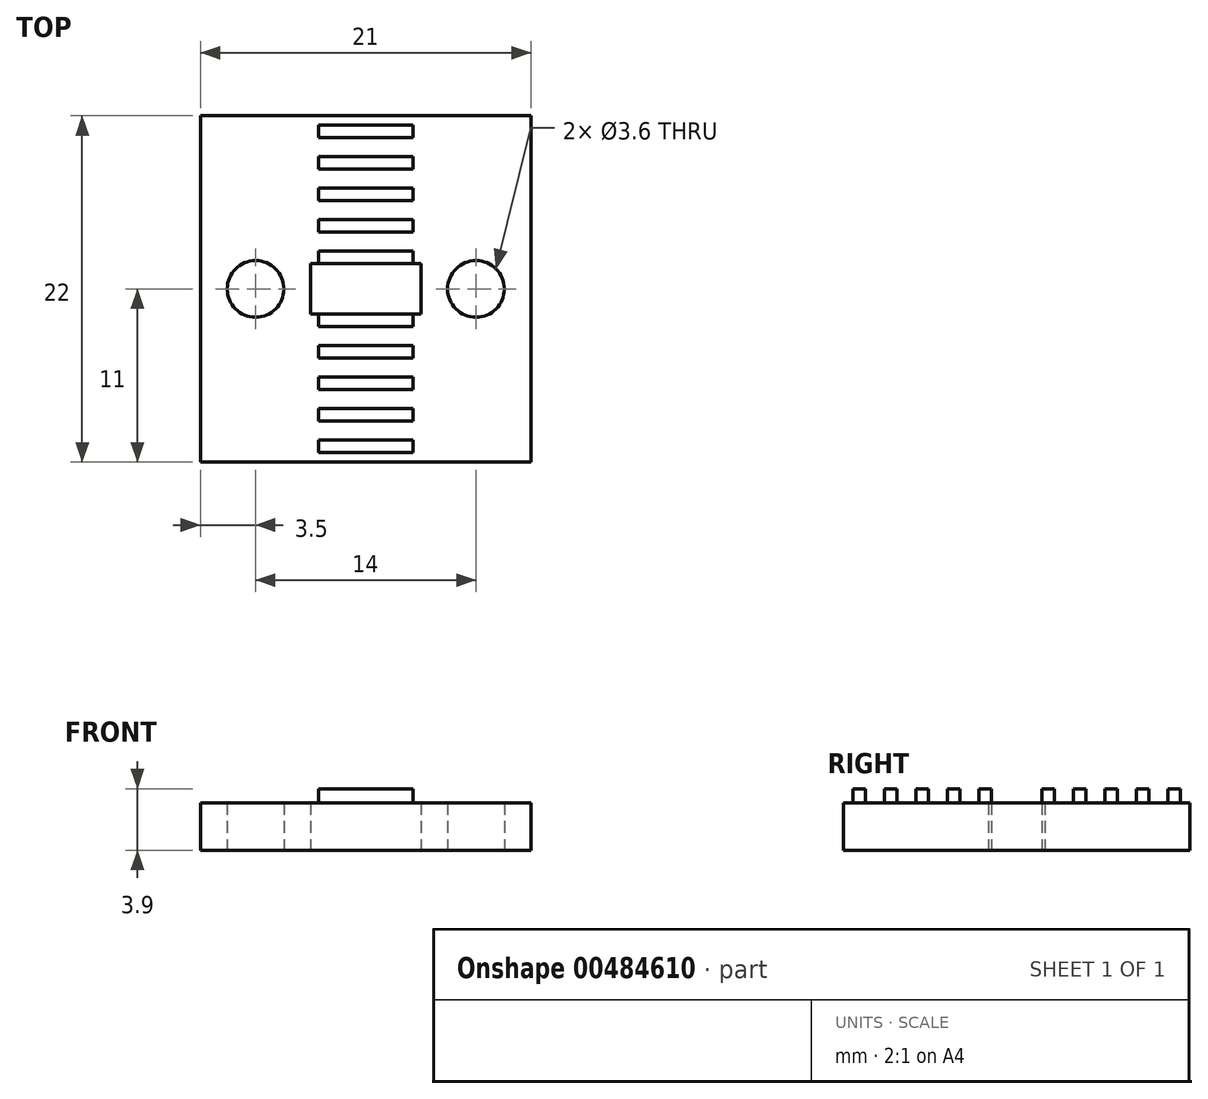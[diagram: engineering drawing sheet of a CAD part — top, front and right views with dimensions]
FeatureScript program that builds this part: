
annotation { "Feature Type Name" : "Feature", "Feature Type Description" : "" }
export const myFeature = defineFeature(function(context is Context, id is Id, definition is map)
    precondition{}
    {
        {
            var Q0;
            Q0=qCreatedBy(makeId("Top.planeOp"),FACE);
            var sketch = newSketch(context, id + "F0", { "sketchPlane" : qUnion([Q0])});
            skLineSegment(sketch, "E0", {"start": v(-20.99, 0) * mm, "end": v(23.9, 0) * mm, "construction": true});
            skCircle(sketch, "E1", {"center": v(-7, 0) * mm, "radius": 1.8 * mm});
            skCircle(sketch, "E2", {"center": v(7, 0) * mm, "radius": 1.8 * mm});
            skLineSegment(sketch, "E3", {"start": v(0, 19.46) * mm, "end": v(0, -20.23) * mm, "construction": true});
            skLineSegment(sketch, "E4.bottom", {"start": v(-3, 0.4) * mm, "end": v(3, 0.4) * mm});
            skLineSegment(sketch, "E4.top", {"start": v(-3, -0.4) * mm, "end": v(3, -0.4) * mm});
            skLineSegment(sketch, "E4.left", {"start": v(-3, 0.4) * mm, "end": v(-3, -0.4) * mm});
            skLineSegment(sketch, "E4.right", {"start": v(3, 0.4) * mm, "end": v(3, -0.4) * mm});
            skLineSegment(sketch, "E5.1.0.0", {"start": v(-3, -2.4) * mm, "end": v(3, -2.4) * mm});
            skLineSegment(sketch, "E5.1.0.1", {"start": v(-3, -1.6) * mm, "end": v(3, -1.6) * mm});
            skLineSegment(sketch, "E5.1.0.2", {"start": v(-3, -1.6) * mm, "end": v(-3, -2.4) * mm});
            skLineSegment(sketch, "E5.1.0.3", {"start": v(3, -1.6) * mm, "end": v(3, -2.4) * mm});
            skLineSegment(sketch, "E5.2.0.0", {"start": v(-3, -4.4) * mm, "end": v(3, -4.4) * mm});
            skLineSegment(sketch, "E5.2.0.1", {"start": v(-3, -3.6) * mm, "end": v(3, -3.6) * mm});
            skLineSegment(sketch, "E5.2.0.2", {"start": v(-3, -3.6) * mm, "end": v(-3, -4.4) * mm});
            skLineSegment(sketch, "E5.2.0.3", {"start": v(3, -3.6) * mm, "end": v(3, -4.4) * mm});
            skLineSegment(sketch, "E5.3.0.0", {"start": v(-3, -6.4) * mm, "end": v(3, -6.4) * mm});
            skLineSegment(sketch, "E5.3.0.1", {"start": v(-3, -5.6) * mm, "end": v(3, -5.6) * mm});
            skLineSegment(sketch, "E5.3.0.2", {"start": v(-3, -5.6) * mm, "end": v(-3, -6.4) * mm});
            skLineSegment(sketch, "E5.3.0.3", {"start": v(3, -5.6) * mm, "end": v(3, -6.4) * mm});
            skLineSegment(sketch, "E5.4.0.0", {"start": v(-3, -8.4) * mm, "end": v(3, -8.4) * mm});
            skLineSegment(sketch, "E5.4.0.1", {"start": v(-3, -7.6) * mm, "end": v(3, -7.6) * mm});
            skLineSegment(sketch, "E5.4.0.2", {"start": v(-3, -7.6) * mm, "end": v(-3, -8.4) * mm});
            skLineSegment(sketch, "E5.4.0.3", {"start": v(3, -7.6) * mm, "end": v(3, -8.4) * mm});
            skLineSegment(sketch, "E5.direction1", {"start": v(-3, -0.4) * mm, "end": v(-3, -2.4) * mm, "construction": true});
            skLineSegment(sketch, "E6.1.0.0", {"start": v(-3, 1.6) * mm, "end": v(3, 1.6) * mm});
            skLineSegment(sketch, "E6.1.0.1", {"start": v(-3, 2.4) * mm, "end": v(3, 2.4) * mm});
            skLineSegment(sketch, "E6.1.0.2", {"start": v(-3, 2.4) * mm, "end": v(-3, 1.6) * mm});
            skLineSegment(sketch, "E6.1.0.3", {"start": v(3, 2.4) * mm, "end": v(3, 1.6) * mm});
            skLineSegment(sketch, "E6.2.0.0", {"start": v(-3, 3.6) * mm, "end": v(3, 3.6) * mm});
            skLineSegment(sketch, "E6.2.0.1", {"start": v(-3, 4.4) * mm, "end": v(3, 4.4) * mm});
            skLineSegment(sketch, "E6.2.0.2", {"start": v(-3, 4.4) * mm, "end": v(-3, 3.6) * mm});
            skLineSegment(sketch, "E6.2.0.3", {"start": v(3, 4.4) * mm, "end": v(3, 3.6) * mm});
            skLineSegment(sketch, "E6.3.0.0", {"start": v(-3, 5.6) * mm, "end": v(3, 5.6) * mm});
            skLineSegment(sketch, "E6.3.0.1", {"start": v(-3, 6.4) * mm, "end": v(3, 6.4) * mm});
            skLineSegment(sketch, "E6.3.0.2", {"start": v(-3, 6.4) * mm, "end": v(-3, 5.6) * mm});
            skLineSegment(sketch, "E6.3.0.3", {"start": v(3, 6.4) * mm, "end": v(3, 5.6) * mm});
            skLineSegment(sketch, "E6.4.0.0", {"start": v(-3, 7.6) * mm, "end": v(3, 7.6) * mm});
            skLineSegment(sketch, "E6.4.0.1", {"start": v(-3, 8.4) * mm, "end": v(3, 8.4) * mm});
            skLineSegment(sketch, "E6.4.0.2", {"start": v(-3, 8.4) * mm, "end": v(-3, 7.6) * mm});
            skLineSegment(sketch, "E6.4.0.3", {"start": v(3, 8.4) * mm, "end": v(3, 7.6) * mm});
            skLineSegment(sketch, "E6.direction1", {"start": v(-3, -0.4) * mm, "end": v(-3, 1.6) * mm, "construction": true});
            skLineSegment(sketch, "E7.bottom", {"start": v(-10.5, 11) * mm, "end": v(10.5, 11) * mm});
            skLineSegment(sketch, "E7.top", {"start": v(-10.5, -11) * mm, "end": v(10.5, -11) * mm});
            skLineSegment(sketch, "E7.left", {"start": v(-10.5, 11) * mm, "end": v(-10.5, -11) * mm});
            skLineSegment(sketch, "E7.right", {"start": v(10.5, 11) * mm, "end": v(10.5, -11) * mm});
            skLineSegment(sketch, "E8.0.5.0", {"start": v(-3, -10.4) * mm, "end": v(3, -10.4) * mm});
            skLineSegment(sketch, "E8.3.5.0", {"start": v(-3, -9.6) * mm, "end": v(3, -9.6) * mm});
            skLineSegment(sketch, "E8.6.5.0", {"start": v(-3, -9.6) * mm, "end": v(-3, -10.4) * mm});
            skLineSegment(sketch, "E8.9.5.0", {"start": v(3, -9.6) * mm, "end": v(3, -10.4) * mm});
            skLineSegment(sketch, "E9.0.5.0", {"start": v(-3, 9.6) * mm, "end": v(3, 9.6) * mm});
            skLineSegment(sketch, "E9.3.5.0", {"start": v(-3, 10.4) * mm, "end": v(3, 10.4) * mm});
            skLineSegment(sketch, "E9.6.5.0", {"start": v(-3, 10.4) * mm, "end": v(-3, 9.6) * mm});
            skLineSegment(sketch, "E9.9.5.0", {"start": v(3, 10.4) * mm, "end": v(3, 9.6) * mm});
            skSolve(sketch);
        }
        {
            var Q0;
            Q0=makeQuery(id+"F0.imprint","IMPRINT",FACE,{"disambiguationData":[TD([[makeQuery(id+"F0.imprint","IMPRINT",EDGE,{"derivedFrom":sQuery(id+"F0.wireOp",EDGE,"E1")}),-1.0]])]});
            extrude(context, id + "F1", {"entities" : qUnion([Q0]), "depth" : 3 * mm, "offsetDistance" : 25 * mm});
        }
        {
            var Q0;
            Q0=makeQuery(id+"F0.imprint","IMPRINT",FACE,{"disambiguationData":[TD([[makeQuery(id+"F0.imprint","IMPRINT",EDGE,{"derivedFrom":sQuery(id+"F0.wireOp",EDGE,"E6.4.0.0")}),1.0]])]});
            var Q1;
            Q1=makeQuery(id+"F0.imprint","IMPRINT",FACE,{"disambiguationData":[TD([[makeQuery(id+"F0.imprint","IMPRINT",EDGE,{"derivedFrom":sQuery(id+"F0.wireOp",EDGE,"E6.3.0.0")}),1.0]])]});
            var Q2;
            Q2=makeQuery(id+"F0.imprint","IMPRINT",FACE,{"disambiguationData":[TD([[makeQuery(id+"F0.imprint","IMPRINT",EDGE,{"derivedFrom":sQuery(id+"F0.wireOp",EDGE,"E6.2.0.0")}),1.0]])]});
            var Q3;
            Q3=makeQuery(id+"F0.imprint","IMPRINT",FACE,{"disambiguationData":[TD([[makeQuery(id+"F0.imprint","IMPRINT",EDGE,{"derivedFrom":sQuery(id+"F0.wireOp",EDGE,"E6.1.0.0")}),1.0]])]});
            var Q4;
            Q4=makeQuery(id+"F0.imprint","IMPRINT",FACE,{"disambiguationData":[TD([[makeQuery(id+"F0.imprint","IMPRINT",EDGE,{"derivedFrom":sQuery(id+"F0.wireOp",EDGE,"E4.bottom")}),-1.0]])]});
            var Q5;
            Q5=makeQuery(id+"F0.imprint","IMPRINT",FACE,{"disambiguationData":[TD([[makeQuery(id+"F0.imprint","IMPRINT",EDGE,{"derivedFrom":sQuery(id+"F0.wireOp",EDGE,"E5.1.0.0")}),1.0]])]});
            var Q6;
            Q6=makeQuery(id+"F0.imprint","IMPRINT",FACE,{"disambiguationData":[TD([[makeQuery(id+"F0.imprint","IMPRINT",EDGE,{"derivedFrom":sQuery(id+"F0.wireOp",EDGE,"E5.2.0.0")}),1.0]])]});
            var Q7;
            Q7=makeQuery(id+"F0.imprint","IMPRINT",FACE,{"disambiguationData":[TD([[makeQuery(id+"F0.imprint","IMPRINT",EDGE,{"derivedFrom":sQuery(id+"F0.wireOp",EDGE,"E5.3.0.0")}),1.0]])]});
            var Q8;
            Q8=makeQuery(id+"F0.imprint","IMPRINT",FACE,{"disambiguationData":[TD([[makeQuery(id+"F0.imprint","IMPRINT",EDGE,{"derivedFrom":sQuery(id+"F0.wireOp",EDGE,"E5.4.0.0")}),1.0]])]});
            var Q9;
            Q9=makeQuery(id+"F0.imprint","IMPRINT",FACE,{"disambiguationData":[TD([[makeQuery(id+"F0.imprint","IMPRINT",EDGE,{"derivedFrom":sQuery(id+"F0.wireOp",EDGE,"E9.0.5.0")}),1.0]])]});
            var Q10;
            Q10=makeQuery(id+"F0.imprint","IMPRINT",FACE,{"disambiguationData":[TD([[makeQuery(id+"F0.imprint","IMPRINT",EDGE,{"derivedFrom":sQuery(id+"F0.wireOp",EDGE,"E8.0.5.0")}),1.0]])]});
            extrude(context, id + "F2", {"entities" : qUnion([Q0, Q1, Q2, Q3, Q4, Q5, Q6, Q7, Q8, Q9, Q10]), "operationType" : NewBodyOperationType.ADD, "offsetDistance" : 25 * mm, "depth" : 3.9 * mm});
        }
        {
            var Q0;
            {var subQ0=sQuery(id+"F0.wireOp",EDGE,"E6.4.0.3");var subQ1=sQuery(id+"F0.wireOp",EDGE,"E6.4.0.2");var subQ2=sQuery(id+"F0.wireOp",EDGE,"E6.4.0.1");var subQ3=sQuery(id+"F0.wireOp",EDGE,"E6.4.0.0");var subQ4=sQuery(id+"F0.wireOp",EDGE,"E6.3.0.3");var subQ5=sQuery(id+"F0.wireOp",EDGE,"E6.3.0.2");var subQ6=sQuery(id+"F0.wireOp",EDGE,"E6.3.0.1");var subQ7=sQuery(id+"F0.wireOp",EDGE,"E6.3.0.0");var subQ8=sQuery(id+"F0.wireOp",EDGE,"E6.2.0.3");var subQ9=sQuery(id+"F0.wireOp",EDGE,"E6.2.0.2");var subQ10=sQuery(id+"F0.wireOp",EDGE,"E6.2.0.1");var subQ11=sQuery(id+"F0.wireOp",EDGE,"E6.2.0.0");var subQ12=sQuery(id+"F0.wireOp",EDGE,"E6.1.0.3");var subQ13=sQuery(id+"F0.wireOp",EDGE,"E6.1.0.2");var subQ14=sQuery(id+"F0.wireOp",EDGE,"E6.1.0.1");var subQ15=sQuery(id+"F0.wireOp",EDGE,"E6.1.0.0");var subQ16=sQuery(id+"F0.wireOp",EDGE,"E5.4.0.3");var subQ17=sQuery(id+"F0.wireOp",EDGE,"E5.4.0.2");var subQ18=sQuery(id+"F0.wireOp",EDGE,"E5.4.0.1");var subQ19=sQuery(id+"F0.wireOp",EDGE,"E5.4.0.0");var subQ20=sQuery(id+"F0.wireOp",EDGE,"E5.3.0.3");var subQ21=sQuery(id+"F0.wireOp",EDGE,"E5.3.0.2");var subQ22=sQuery(id+"F0.wireOp",EDGE,"E5.3.0.1");var subQ23=sQuery(id+"F0.wireOp",EDGE,"E5.3.0.0");var subQ24=sQuery(id+"F0.wireOp",EDGE,"E5.2.0.3");var subQ25=sQuery(id+"F0.wireOp",EDGE,"E5.2.0.2");var subQ26=sQuery(id+"F0.wireOp",EDGE,"E5.2.0.1");var subQ27=sQuery(id+"F0.wireOp",EDGE,"E5.2.0.0");var subQ28=sQuery(id+"F0.wireOp",EDGE,"E5.1.0.3");var subQ29=sQuery(id+"F0.wireOp",EDGE,"E5.1.0.2");var subQ30=sQuery(id+"F0.wireOp",EDGE,"E5.1.0.1");var subQ31=sQuery(id+"F0.wireOp",EDGE,"E5.1.0.0");var subQ32=sQuery(id+"F0.wireOp",EDGE,"E4.right");var subQ33=sQuery(id+"F0.wireOp",EDGE,"E4.left");var subQ34=sQuery(id+"F0.wireOp",EDGE,"E4.top");var subQ35=sQuery(id+"F0.wireOp",EDGE,"E4.bottom");Q0=makeQuery(id+"F2.boolean.opBoolean","MERGE",FACE,{"derivedFrom":[makeQuery(id+"F1.opExtrude","CAP_FACE",FACE,{"disambiguationData":[OSD([sQuery(id+"F0.wireOp",EDGE,"E1"),sQuery(id+"F0.wireOp",EDGE,"E2"),subQ35,subQ34,subQ33,subQ32,subQ31,subQ30,subQ29,subQ28,subQ27,subQ26,subQ25,subQ24,subQ23,subQ22,subQ21,subQ20,subQ19,subQ18,subQ17,subQ16,subQ15,subQ14,subQ13,subQ12,subQ11,subQ10,subQ9,subQ8,subQ7,subQ6,subQ5,subQ4,subQ3,subQ2,subQ1,subQ0,sQuery(id+"F0.wireOp",EDGE,"E7.bottom"),sQuery(id+"F0.wireOp",EDGE,"E7.top"),sQuery(id+"F0.wireOp",EDGE,"E7.left"),sQuery(id+"F0.wireOp",EDGE,"E7.right")])],"isStart":true}),makeQuery(id+"F2.opExtrude","CAP_FACE",FACE,{"disambiguationData":[OSD([subQ35,subQ34,subQ33,subQ32])],"isStart":true}),makeQuery(id+"F2.opExtrude","CAP_FACE",FACE,{"disambiguationData":[OSD([subQ31,subQ30,subQ29,subQ28])],"isStart":true}),makeQuery(id+"F2.opExtrude","CAP_FACE",FACE,{"disambiguationData":[OSD([subQ27,subQ26,subQ25,subQ24])],"isStart":true}),makeQuery(id+"F2.opExtrude","CAP_FACE",FACE,{"disambiguationData":[OSD([subQ23,subQ22,subQ21,subQ20])],"isStart":true}),makeQuery(id+"F2.opExtrude","CAP_FACE",FACE,{"disambiguationData":[OSD([subQ19,subQ18,subQ17,subQ16])],"isStart":true}),makeQuery(id+"F2.opExtrude","CAP_FACE",FACE,{"disambiguationData":[OSD([subQ15,subQ14,subQ13,subQ12])],"isStart":true}),makeQuery(id+"F2.opExtrude","CAP_FACE",FACE,{"disambiguationData":[OSD([subQ11,subQ10,subQ9,subQ8])],"isStart":true}),makeQuery(id+"F2.opExtrude","CAP_FACE",FACE,{"disambiguationData":[OSD([subQ7,subQ6,subQ5,subQ4])],"isStart":true}),makeQuery(id+"F2.opExtrude","CAP_FACE",FACE,{"disambiguationData":[OSD([subQ3,subQ2,subQ1,subQ0])],"isStart":true})]});}
            var sketch = newSketch(context, id + "F3", { "sketchPlane" : qUnion([Q0])});
            skLineSegment(sketch, "E10.0", {"start": v(0, -19.46) * mm, "end": v(0, 20.23) * mm, "construction": true});
            skLineSegment(sketch, "E10.1", {"start": v(-20.99, 0) * mm, "end": v(23.9, 0) * mm, "construction": true});
            skLineSegment(sketch, "E11.bottom", {"start": v(-3.5, 1.6) * mm, "end": v(3.5, 1.6) * mm});
            skLineSegment(sketch, "E11.top", {"start": v(-3.5, -1.6) * mm, "end": v(3.5, -1.6) * mm});
            skLineSegment(sketch, "E11.left", {"start": v(-3.5, 1.6) * mm, "end": v(-3.5, -1.6) * mm});
            skLineSegment(sketch, "E11.right", {"start": v(3.5, 1.6) * mm, "end": v(3.5, -1.6) * mm});
            skSolve(sketch);
        }
        {
            var Q0;
            Q0=makeQuery(id+"F3.imprint","IMPRINT",FACE,{"disambiguationData":[TD([[makeQuery(id+"F3.imprint","IMPRINT",EDGE,{"derivedFrom":sQuery(id+"F3.wireOp",EDGE,"E11.bottom")}),-1.0]])]});
            extrude(context, id + "F4", {"entities" : qUnion([Q0]), "operationType" : NewBodyOperationType.REMOVE, "oppositeDirection" : true, "depth" : 25 * mm});
        }
    });
